# Revit family: HAKRTYP001
name_source: partatom
category: Furniture
units: mm (PartAtom-declared; Revit-internal decimal feet)

## family parameters
Always vertical = Yes
Cut with Voids When Loaded = No
OmniClass Number = 23.40.20.00
OmniClass Title = General Furniture and Specialties
Render Appearance Source = Family Geometry
Room Calculation Point = No
Shared = No
Work Plane-Based = No

## types (1)
- HAKRTYP001
    Cost = 19664 $
    Default Elevation = 0 mm  [stored 0 ft]
    Description = 2 x Hakr Lounge w/Ledge 3-Seater, 72" W, Configurable, 1 x Hakr Lounge w/Ledge, Round Corner, 90-degree, Configurable, 4 x Juggle Chair, 5-Star Swivel Base on Casters, 1 x Hakr Square Table
    Exported From CET Designer = Yes
    Manufacturer = AIS
    Model = LHKRLL3C
    Show HAKRTYP001 = Yes
    VisibilityIndex = 0

note: [stored X ft] marks values corroborated as IEEE doubles in the binary element streams (Revit-internal decimal feet)

## geometry (parser evidence)
native form markers: Sweep x3
no freeform markers — native parametric forms only
